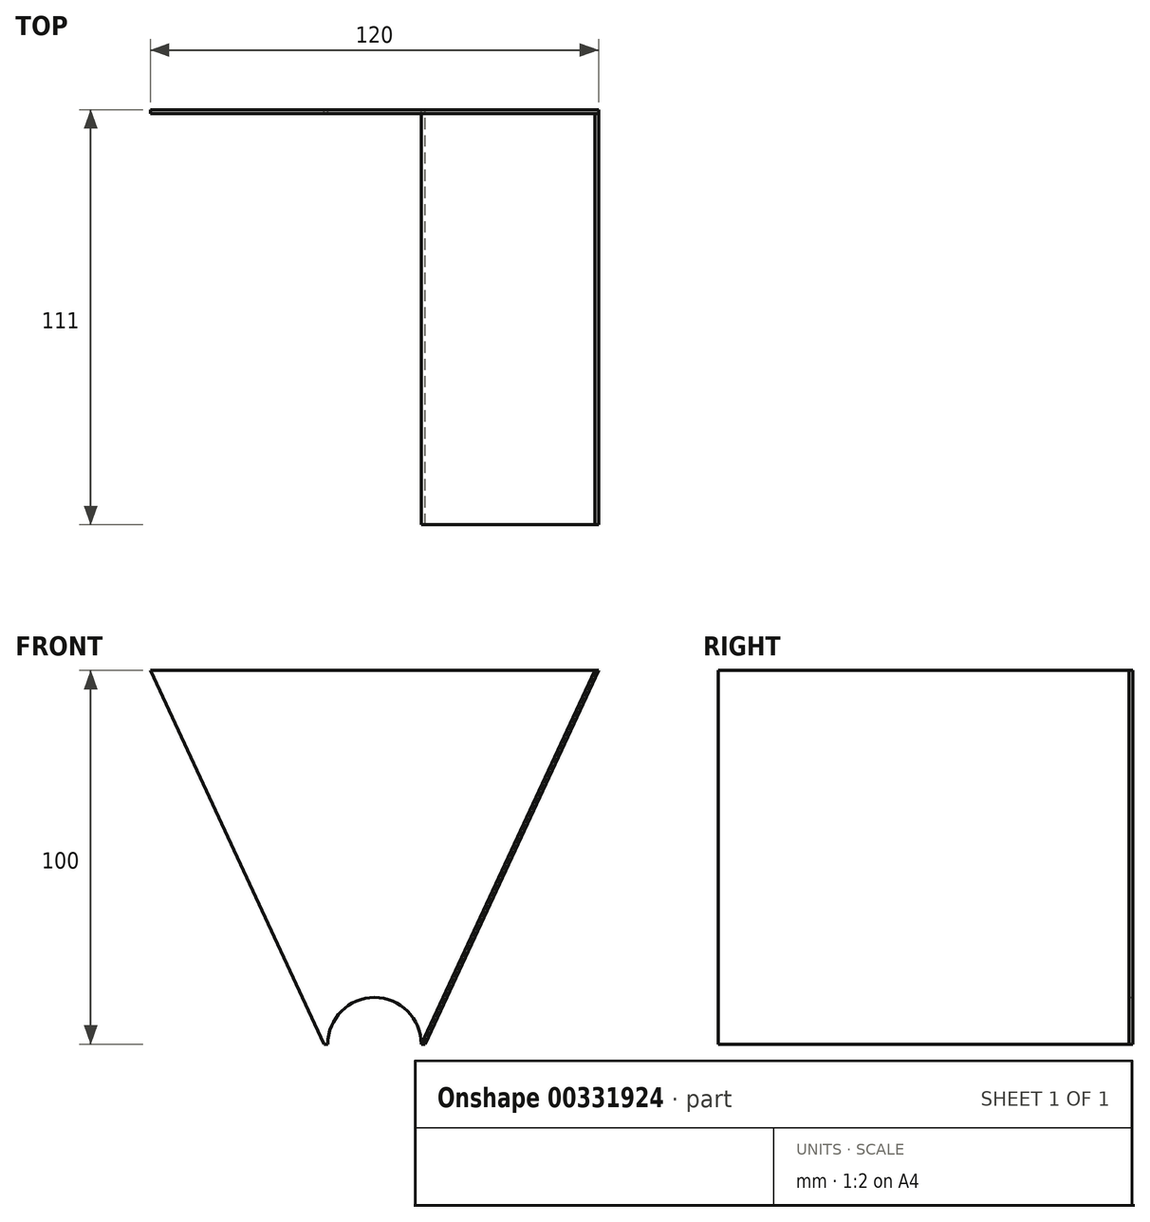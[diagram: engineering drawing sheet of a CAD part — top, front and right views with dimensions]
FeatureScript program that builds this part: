
annotation { "Feature Type Name" : "Feature", "Feature Type Description" : "" }
export const myFeature = defineFeature(function(context is Context, id is Id, definition is map)
    precondition{}
    {
        {
            var Q0;
            Q0=qCreatedBy(makeId("Front.planeOp"),FACE);
            var sketch = newSketch(context, id + "F0", { "sketchPlane" : qUnion([Q0])});
            skLineSegment(sketch, "E0", {"start": v(-60, 50) * mm, "end": v(60, 50) * mm});
            skLineSegment(sketch, "E1", {"start": v(60, 50) * mm, "end": v(13.5, -50) * mm});
            skLineSegment(sketch, "E2", {"start": v(13.5, -50) * mm, "end": v(-13.5, -50) * mm});
            skLineSegment(sketch, "E3", {"start": v(-13.5, -50) * mm, "end": v(-60, 50) * mm});
            skCircle(sketch, "E4", {"center": v(0, -50) * mm, "radius": 12.5 * mm});
            skPoint(sketch, "E5", {"position": v(0, 50) * mm});
            skSolve(sketch);
        }
        {
            var Q0;
            Q0=makeQuery(id+"F0.imprint","IMPRINT",FACE,{"disambiguationData":[TD([[makeQuery(id+"F0.imprint","IMPRINT",EDGE,{"derivedFrom":sQuery(id+"F0.wireOp",EDGE,"E0")}),-1.0]])]});
            extrude(context, id + "F1", {"entities" : qUnion([Q0]), "depth" : 1 * mm});
        }
        {
            var Q0;
            Q0=makeQuery(id+"F1.opExtrude","CAP_FACE",FACE,{"disambiguationData":[OSD([sQuery(id+"F0.wireOp",EDGE,"E0"),sQuery(id+"F0.wireOp",EDGE,"E1"),sQuery(id+"F0.wireOp",EDGE,"E2"),sQuery(id+"F0.wireOp",EDGE,"E3"),sQuery(id+"F0.wireOp",EDGE,"E4")])],"isStart":false});
            var sketch = newSketch(context, id + "F2", { "sketchPlane" : qUnion([Q0])});
            skLineSegment(sketch, "E6.0", {"start": v(60, 50) * mm, "end": v(13.5, -50) * mm});
            skLineSegment(sketch, "E7", {"start": v(60, 50) * mm, "end": v(59, 50) * mm});
            skLineSegment(sketch, "E8", {"start": v(59, 50) * mm, "end": v(12.5, -50) * mm});
            skLineSegment(sketch, "E9", {"start": v(12.5, -50) * mm, "end": v(13.5, -50) * mm});
            skSolve(sketch);
        }
        {
            var Q0;
            Q0 = qSketchRegion(id + "F2", true);
            extrude(context, id + "F3", {"entities" : qUnion([Q0]), "depth" : 110 * mm});
        }
    });
